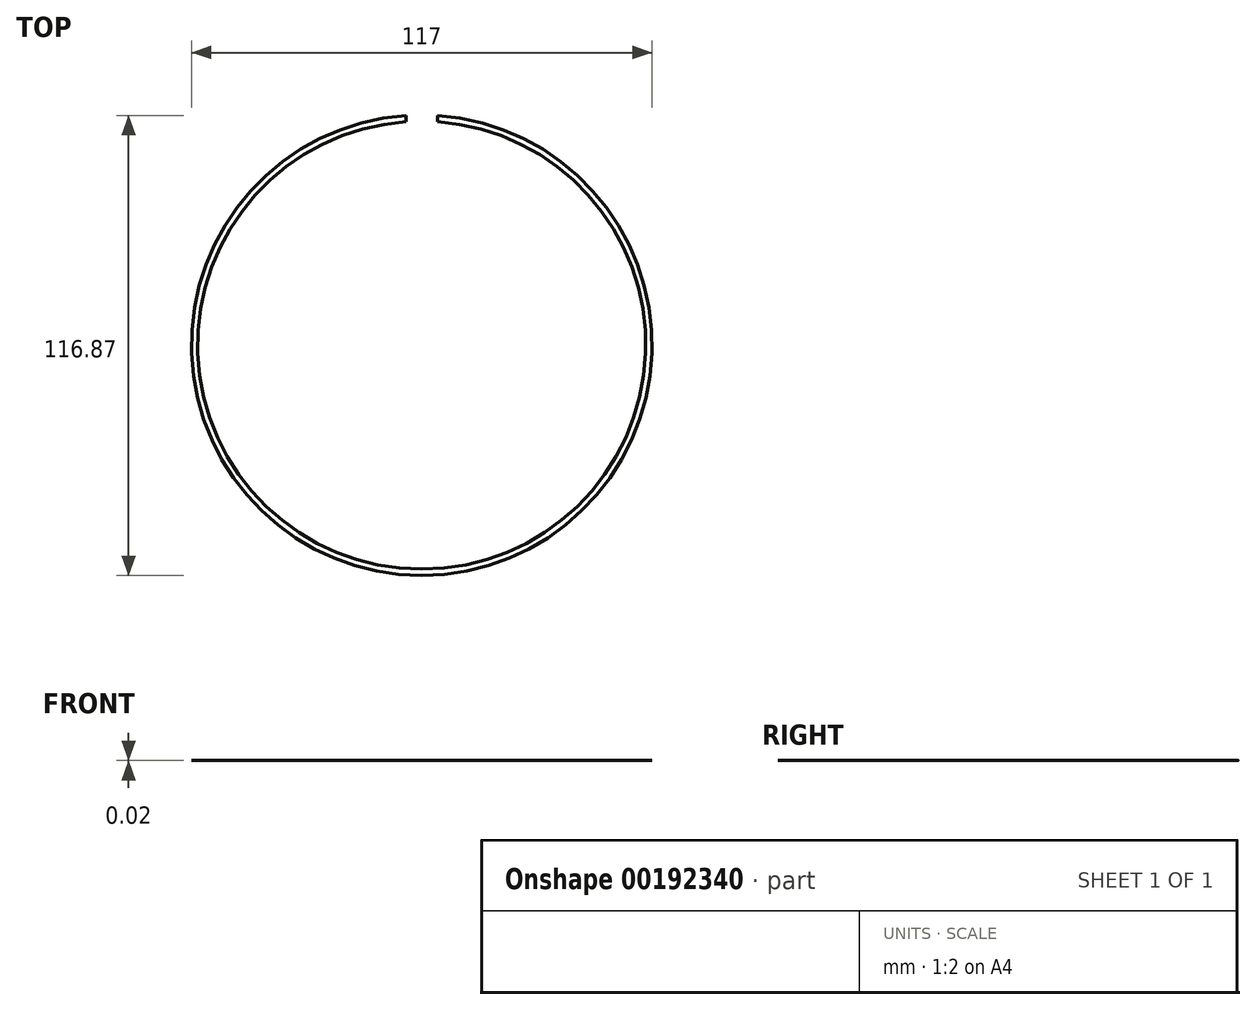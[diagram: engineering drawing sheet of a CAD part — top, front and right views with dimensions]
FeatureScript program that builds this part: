
annotation { "Feature Type Name" : "Feature", "Feature Type Description" : "" }
export const myFeature = defineFeature(function(context is Context, id is Id, definition is map)
    precondition{}
    {
        {
            var Q0;
            Q0=qCreatedBy(makeId("Top.planeOp"),FACE);
            var sketch = newSketch(context, id + "F0", { "sketchPlane" : qUnion([Q0])});
            skCircle(sketch, "E0", {"center": v(0, 0) * mm, "radius": 63.5 * mm});
            skCircle(sketch, "E1.0", {"center": v(0, 0) * mm, "radius": 58.5 * mm});
            skCircle(sketch, "E2.0", {"center": v(0, 0) * mm, "radius": 56.91 * mm});
            skSolve(sketch);
        }
        {
            var Q0;
            Q0=makeQuery(id+"F0.imprint","IMPRINT",FACE,{"disambiguationData":[TD([[makeQuery(id+"F0.imprint","IMPRINT",EDGE,{"derivedFrom":sQuery(id+"F0.wireOp",EDGE,"E1.0")}),1.0]])]});
            extrude(context, id + "F1", {"entities" : qUnion([Q0]), "depth" : 5 / 203.2 * mm});
        }
        {
            var Q0;
            Q0=qCreatedBy(makeId("Front.planeOp"),FACE);
            var sketch = newSketch(context, id + "F2", { "sketchPlane" : qUnion([Q0])});
            skLineSegment(sketch, "E3.0", {"start": v(0, 11.11) * mm, "end": v(-24.4, 11.11) * mm});
            skLineSegment(sketch, "E4.0", {"start": v(0, 7.94) * mm, "end": v(-24.4, 7.94) * mm});
            skLineSegment(sketch, "E5.MirrorCS", {"start": v(0, 7.94) * mm, "end": v(24.4, 7.94) * mm});
            skLineSegment(sketch, "E6.MirrorCS", {"start": v(0, 11.11) * mm, "end": v(24.4, 11.11) * mm});
            skLineSegment(sketch, "E7", {"start": v(-25.4, 10.11) * mm, "end": v(-25.4, 8.94) * mm});
            skLineSegment(sketch, "E8", {"start": v(25.4, 10.11) * mm, "end": v(25.4, 8.94) * mm});
            skPoint(sketch, "E9.visualSharp", {"position": v(-25.4, 11.11) * mm});
            skArc(sketch, "E9.filletArc", {"start": v(-24.4, 11.11) * mm, "mid": v(-25.11, 10.82) * mm, "end": v(-25.4, 10.11) * mm});
            skPoint(sketch, "E10.visualSharp", {"position": v(-25.4, 7.94) * mm});
            skArc(sketch, "E10.filletArc", {"start": v(-25.4, 8.94) * mm, "mid": v(-25.11, 8.23) * mm, "end": v(-24.4, 7.94) * mm});
            skPoint(sketch, "E11.visualSharp", {"position": v(25.4, 11.11) * mm});
            skArc(sketch, "E11.filletArc", {"start": v(25.4, 10.11) * mm, "mid": v(25.11, 10.82) * mm, "end": v(24.4, 11.11) * mm});
            skPoint(sketch, "E12.visualSharp", {"position": v(25.4, 7.94) * mm});
            skArc(sketch, "E12.filletArc", {"start": v(24.4, 7.94) * mm, "mid": v(25.11, 8.23) * mm, "end": v(25.4, 8.94) * mm});
            skSolve(sketch);
        }
        {
            var Q0;
            Q0 = qSketchRegion(id + "F2", true);
            extrude(context, id + "F3", {"entities" : qUnion([Q0]), "operationType" : NewBodyOperationType.REMOVE, "depth" : 62 * mm});
        }
        {
            var Q0;
            Q0=qCreatedBy(makeId("Front.planeOp"),FACE);
            var sketch = newSketch(context, id + "F4", { "sketchPlane" : qUnion([Q0])});
            skLineSegment(sketch, "E13", {"start": v(0, 0) * mm, "end": v(0, 6.35) * mm});
            skLineSegment(sketch, "E14", {"start": v(0, 6.35) * mm, "end": v(-3.17, 6.35) * mm});
            skLineSegment(sketch, "E15", {"start": v(-3.17, 6.35) * mm, "end": v(-3.97, 0) * mm});
            skLineSegment(sketch, "E16.MirrorCS", {"start": v(0, 6.35) * mm, "end": v(3.17, 6.35) * mm});
            skLineSegment(sketch, "E17.MirrorCS", {"start": v(3.17, 6.35) * mm, "end": v(3.97, 0) * mm});
            skLineSegment(sketch, "E18", {"start": v(-3.97, 0) * mm, "end": v(3.97, 0) * mm});
            skLineSegment(sketch, "E19", {"start": v(-0.8, 6.35) * mm, "end": v(-0.8, 16.08) * mm});
            skLineSegment(sketch, "E20", {"start": v(-0.8, 16.08) * mm, "end": v(0, 16.08) * mm});
            skLineSegment(sketch, "E21.MirrorCS", {"start": v(0.8, 6.35) * mm, "end": v(0.8, 16.08) * mm});
            skLineSegment(sketch, "E22.MirrorCS", {"start": v(0.8, 16.08) * mm, "end": v(0, 16.08) * mm});
            skSolve(sketch);
        }
        {
            var Q0;
            {var subQ0=sQuery(id+"F4.wireOp",EDGE,"E13");Q0=makeQuery(id+"F4.imprint","IMPRINT",FACE,{"disambiguationData":[TD([[makeQuery(id+"F4.imprint","IMPRINT",EDGE,{"derivedFrom":subQ0}),-1.0]])]});}
            var Q1;
            {var subQ0=sQuery(id+"F4.wireOp",EDGE,"E13");Q1=makeQuery(id+"F4.imprint","IMPRINT",FACE,{"disambiguationData":[TD([[makeQuery(id+"F4.imprint","IMPRINT",EDGE,{"derivedFrom":subQ0}),1.0]])]});}
            var Q2;
            {var subQ0=sQuery(id+"F4.wireOp",EDGE,"E19");Q2=makeQuery(id+"F4.imprint","IMPRINT",FACE,{"disambiguationData":[TD([[makeQuery(id+"F4.imprint","IMPRINT",EDGE,{"derivedFrom":subQ0}),-1.0]])]});}
            extrude(context, id + "F5", {"entities" : qUnion([Q0, Q1, Q2]), "operationType" : NewBodyOperationType.REMOVE, "oppositeDirection" : true, "depth" : 61 * mm});
        }
        {
            var Q0;
            Q0=qCreatedBy(makeId("Right.planeOp"),FACE);
            var sketch = newSketch(context, id + "F6", { "sketchPlane" : qUnion([Q0])});
            skCircle(sketch, "E23", {"center": v(0, 7.94) * mm, "radius": 3.18 * mm});
            skLineSegment(sketch, "E24", {"start": v(0, 15.88) * mm, "end": v(0, 0) * mm});
            skSolve(sketch);
        }
        {
            var Q0;
            Q0 = qSketchRegion(id + "F6", true);
            extrude(context, id + "F7", {"entities" : qUnion([Q0]), "endBound" : BoundingType.SYMMETRIC, "depth" : 161 * mm});
        }
        {
            var Q0;
            Q0=makeQuery(id+"F7.opExtrude","SWEPT_BODY",BODY,{"disambiguationData":[OSD([sQuery(id+"F6.wireOp",EDGE,"E23")])]});
            var Q1;
            Q1=qCreatedBy(makeId("Origin.pointOp"),VERTEX);
            var Q2;
            Q2=makeQuery(id+"F1.opExtrude","SWEPT_FACE",FACE,{"disambiguationData":[OSD([sQuery(id+"F0.wireOp",EDGE,"E1.0")])]});
            transform(context, id + "F8", {"entities" : qUnion([Q0]), "transformType" : TransformType.ROTATION, "transformAxis" : qUnion([Q2]), "angle" : 45 * degree, "makeCopy" : false});
        }
        {
            var Q0;
            Q0=makeQuery(id+"F7.opExtrude","SWEPT_BODY",BODY,{"disambiguationData":[OSD([sQuery(id+"F6.wireOp",EDGE,"E23")])]});
            var Q1;
            Q1=qCreatedBy(makeId("Right.planeOp"),FACE);
            mirror(context, id + "F9", {"entities" : qUnion([Q0]), "mirrorPlane" : qUnion([Q1])});
        }
        {
            var Q0;
            Q0=makeQuery(id+"F9.opPattern","COPY",BODY,{"derivedFrom":makeQuery(id+"F7.opExtrude","SWEPT_BODY",BODY,{"disambiguationData":[OSD([sQuery(id+"F6.wireOp",EDGE,"E23")])]}),"instanceName":"1"});
            var Q1;
            Q1=makeQuery(id+"F7.opExtrude","SWEPT_BODY",BODY,{"disambiguationData":[OSD([sQuery(id+"F6.wireOp",EDGE,"E23")])]});
            var Q2;
            Q2=makeQuery(id+"F1.opExtrude","SWEPT_BODY",BODY,{"disambiguationData":[OSD([sQuery(id+"F0.wireOp",EDGE,"E1.0"),sQuery(id+"F0.wireOp",EDGE,"E2.0")])]});
            booleanBodies(context, id + "F10", {"operationType" : BooleanOperationType.SUBTRACTION, "tools" : qUnion([Q0, Q1]), "targets" : qUnion([Q2])});
        }
    });
